# Revit family: 1003F(2017)
name_source: partatom
category: Plumbing Fixtures
units: mm (PartAtom-declared; Revit-internal decimal feet)

## family parameters
Always vertical = Yes
Cut with Voids When Loaded = No
OmniClass Number = 23.45.55.00
OmniClass Title = Sanitary Faucets, Wastes
Part Type = Normal
Room Calculation Point = No
Round Connector Dimension = Use Diameter
Shared = No
Work Plane-Based = No

## types (1)
- 1003F Washbasin faucet for summer house
    2D/3D/BIM Files URL = http://static.oras.com
    3D View = https://static.oras.com
    Advanced Features = 3S-installation system for safe and simple mounting
    AssetType = Fixed
    BIMObjectName = 1003F(2017)
    Backflow Prevention EN1717 = AA
    BodyMaterial = Brass
    Brand = Oras
    Catalog Drawing URL = http://static.oras.com
    Category B2C = Washbasin
    CloseOffRating = 0
    Color = Chrome
    Connection = Flexible inlet pipes
    Connection Size = G3/8
    Default Elevation = 0 mm  [stored 0 ft]
    Dimension Drawing URL = http://static.oras.com
    DurationUnit = Year
    EAN Number = 6414150078538
    EN Standard = EN 817
    ETIM Class Number = EC011328 Washbasin mixing tap
    Extensions = Water heater unit;Chain holder without chain
    FDV Document URL = http://www.oras.com
    FaucetMainMaterial = Brass
    FaucetNominalDepth = 144 mm  [stored 0.472441 ft]
    FaucetNominalHeight = 147 mm
    FaucetNominalWidth = 58 mm  [stored 0.190289 ft]
    Features = Single-lever;Low pressure
    Finish = Polished
    Flow Drawing URL = http://static.oras.com
    Flow Rate At 300kPa = 0.1 L/s
    FlowCoefficient = 0
    Group = Washbasin faucet
    HWFU = 0
    HeaterNominalDepth = 213 mm
    HeaterNominalHeight = 418 mm
    HeaterNominalWidth = 255 mm
    IfcExportAs = IfcValveType
    IfcExportType = FAUCET
    InletConnectionSize = 10 mm  [stored 0.0328084 ft]
    Installation Type = Deck mounted
    Installation and Maintenance Guide URL = http://static.oras.com
    Interactive AR View URL = https://static.oras.com
    LVI Number = 6110193
    Lever Handle = Single operating lever/handle;Hot/Cold symbols
    Long Marketing = Washbasin faucet for summer house and water heater. Fixed spout and aerator. Maximum flow-rate 5 l/min. Due to the heating of water, water dripping from the aerator is a feature of this product and should not prevented. The aerator may not be changed or supplemented with additional components. Plug in, unpressurized water heater, 5 l. Easy to install. Range of use +35° – 85°C (recommendation + 65°C). In order to prevent frost damage, the faucet and the water heater must be emptied. This water heater is only allowed to operate with the original Oras summer house faucet. Warning! Water heater can heat the water up to +85°C. Beware of the instant scalding hot water from the faucet. The faucet and the water heater should not be installed separately.
    Manufacturer = Oras
    ManufacturerName = Oras
    ManufacturerURL = http://www.oras.com
    Market = International;Denmark;Estonia;Finland;Latvia;Lithuania;Norway;Poland;Russia;Sweden;Ukraine
    Material = Brass
    Max. Hot Water Supply = 70 °C
    Mechanical Parts = Litter filter(s);ø 40 mm ceramic cartridge for flow and temperature control
    Mobile Product Information URL = http://mpi.oras.com
    Model = 1003F Washbasin faucet for summer house
    ModelReference = 1003F
    Mounting Holes = 1 hole
    NBSDescription = Water supply fittings for wash basins and troughs
    NBSReference = 45-35-70/371
    NRF Number = 4200167
    Name = 1003F Washbasin faucet for summer house
    Name_en = 1003F Washbasin faucet for summer house
    Noise Class = I (ISO 3822)
    Pressure Loss With Flow 01ls = 435000.0 Pa
    Product Code = 1003F
    Product Family = Oras Safira
    Product Image URL = http://static.oras.com
    Product URL = http://static.oras.com
    ProductInformation = Washbasin faucet with disinfection wash proof Bidetta shower set
    RSK Number = 8277678
    Sales Package dimensions (LxWxH) = 456 x 275 x 308
    Shape = Sculptured
    Size = Faucet: 58x144x147 mm / Heater: 255x213x418 mm
    Spare-Part Information URL = http://static.oras.com
    Spout Projection = 107 mm
    Spout Type = Fixed spout
    Surface treatment = Chrome
    Technical DataSheet URL = http://www.oras.com
    Temperature = Temperature limiter
    Temperature Adjustments = Limitation option for maximum temperature and flow-rate
    UNSPSC Class Number = 30181700 Faucets or taps
    URL Declaration Of Performance (DOP) = http://static.oras.com
    URL Declaration of Asbestos = http://static.oras.com
    URL Declaration of Conformity = http://static.oras.com
    URL Declaration of SCIP = http://static.oras.com
    URL EU Packaging Declaration = http://static.oras.com
    URL EcoLabel Declaration = http://static.oras.com
    URL REACH = http://static.oras.com
    URL UWL = http://static.oras.com
    Uniclass2 = Pr_40_30_96_96
    Uniclass2015Description = Washbasin manual water supply sets
    Uniclass2015Reference = Pr_40_20_87_96
    Usage Group = Sweden
    VVS Number = 701645604
    Version = 1
    VersionDate = 20/08/2024
    Warranty Information URL = http://warranty.oras.com
    WarrantyDescription = http://warranty.oras.com
    WarrantyDurationUnit = Year
    Working Pressure = 50 - 1000 kPa

note: [stored X ft] marks values corroborated as IEEE doubles in the binary element streams (Revit-internal decimal feet)

## geometry (parser evidence)
native form markers: Sweep x11
no freeform markers — native parametric forms only
